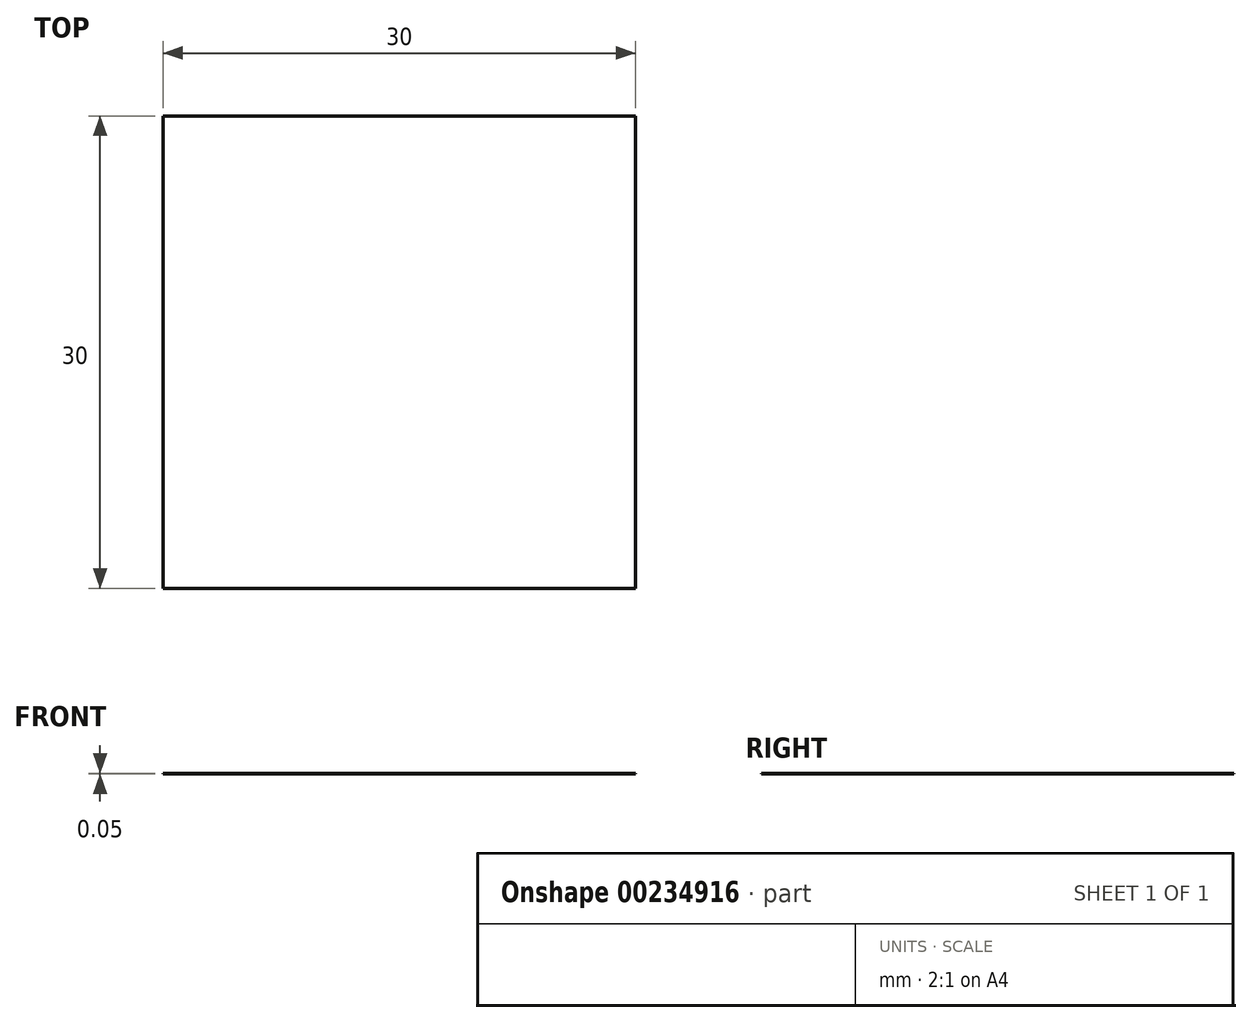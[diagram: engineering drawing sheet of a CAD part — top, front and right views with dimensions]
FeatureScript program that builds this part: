
annotation { "Feature Type Name" : "Feature", "Feature Type Description" : "" }
export const myFeature = defineFeature(function(context is Context, id is Id, definition is map)
    precondition{}
    {
        {
            var Q0;
            Q0=qCreatedBy(makeId("Top.planeOp"),FACE);
            var sketch = newSketch(context, id + "F0", { "sketchPlane" : qUnion([Q0])});
            skLineSegment(sketch, "E0.bottom", {"start": v(15, 15) * mm, "end": v(-15, 15) * mm});
            skLineSegment(sketch, "E0.top", {"start": v(15, -15) * mm, "end": v(-15, -15) * mm});
            skLineSegment(sketch, "E0.left", {"start": v(15, 15) * mm, "end": v(15, -15) * mm});
            skLineSegment(sketch, "E0.right", {"start": v(-15, 15) * mm, "end": v(-15, -15) * mm});
            skPoint(sketch, "E0.middle", {"position": v(0, 0) * mm});
            skSolve(sketch);
        }
        {
            var Q0;
            Q0 = qSketchRegion(id + "F0", true);
            extrude(context, id + "F1", {"entities" : qUnion([Q0]), "depth" : 0.05 * mm});
        }
    });
